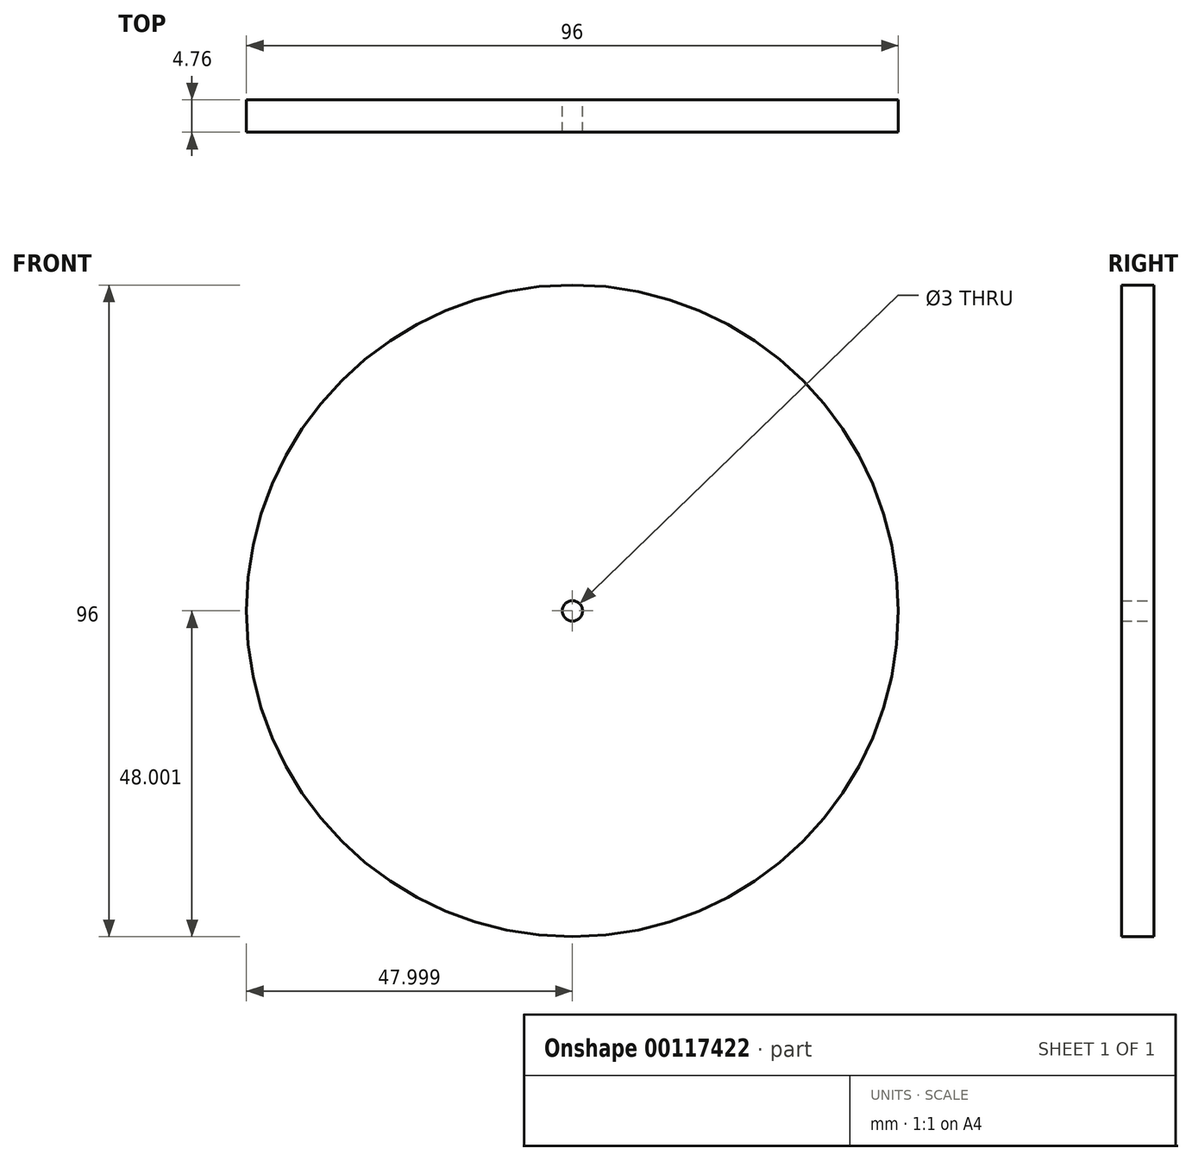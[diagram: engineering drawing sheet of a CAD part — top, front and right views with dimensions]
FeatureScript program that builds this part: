
annotation { "Feature Type Name" : "Feature", "Feature Type Description" : "" }
export const myFeature = defineFeature(function(context is Context, id is Id, definition is map)
    precondition{}
    {
        {
            var Q0;
            Q0=qCreatedBy(makeId("Front.planeOp"),FACE);
            var sketch = newSketch(context, id + "F0", { "sketchPlane" : qUnion([Q0])});
            skCircle(sketch, "E0", {"center": v(-34.72, 19.02) * mm, "radius": 48 * mm});
            skCircle(sketch, "E1", {"center": v(-34.72, 19.02) * mm, "radius": 1500 * mm});
            skCircle(sketch, "E2", {"center": v(-34.72, 19.02) * mm, "radius": 1.5 * mm});
            skSolve(sketch);
        }
        {
            var Q0;
            Q0=makeQuery(id+"F0.imprint","IMPRINT",FACE,{"disambiguationData":[TD([[makeQuery(id+"F0.imprint","IMPRINT",EDGE,{"derivedFrom":sQuery(id+"F0.wireOp",EDGE,"J6k7ENYa-x67j-1Je3-90NJ-yXM5SmYILDOo")}),1.0]])]});
            var Q1;
            Q1=makeQuery(id+"F0.imprint","IMPRINT",FACE,{"disambiguationData":[TD([[makeQuery(id+"F0.imprint","IMPRINT",EDGE,{"derivedFrom":sQuery(id+"F0.wireOp",EDGE,"E0")}),1.0]])]});
            var Q2;
            Q2=sQuery(id+"F0.wireOp",EDGE,"AX3cV3Cy-B1Yd-LhUJ-RWtg-JiZ0P6zwKTnP");
            var Q3;
            Q3=sQuery(id+"F0.wireOp",EDGE,"J6k7ENYa-x67j-1Je3-90NJ-yXM5SmYILDOo");
            extrude(context, id + "F1", {"entities" : qUnion([Q0, Q1]), "surfaceEntities" : qUnion([Q2, Q3]), "depth" : 4.76 * mm});
        }
    });
